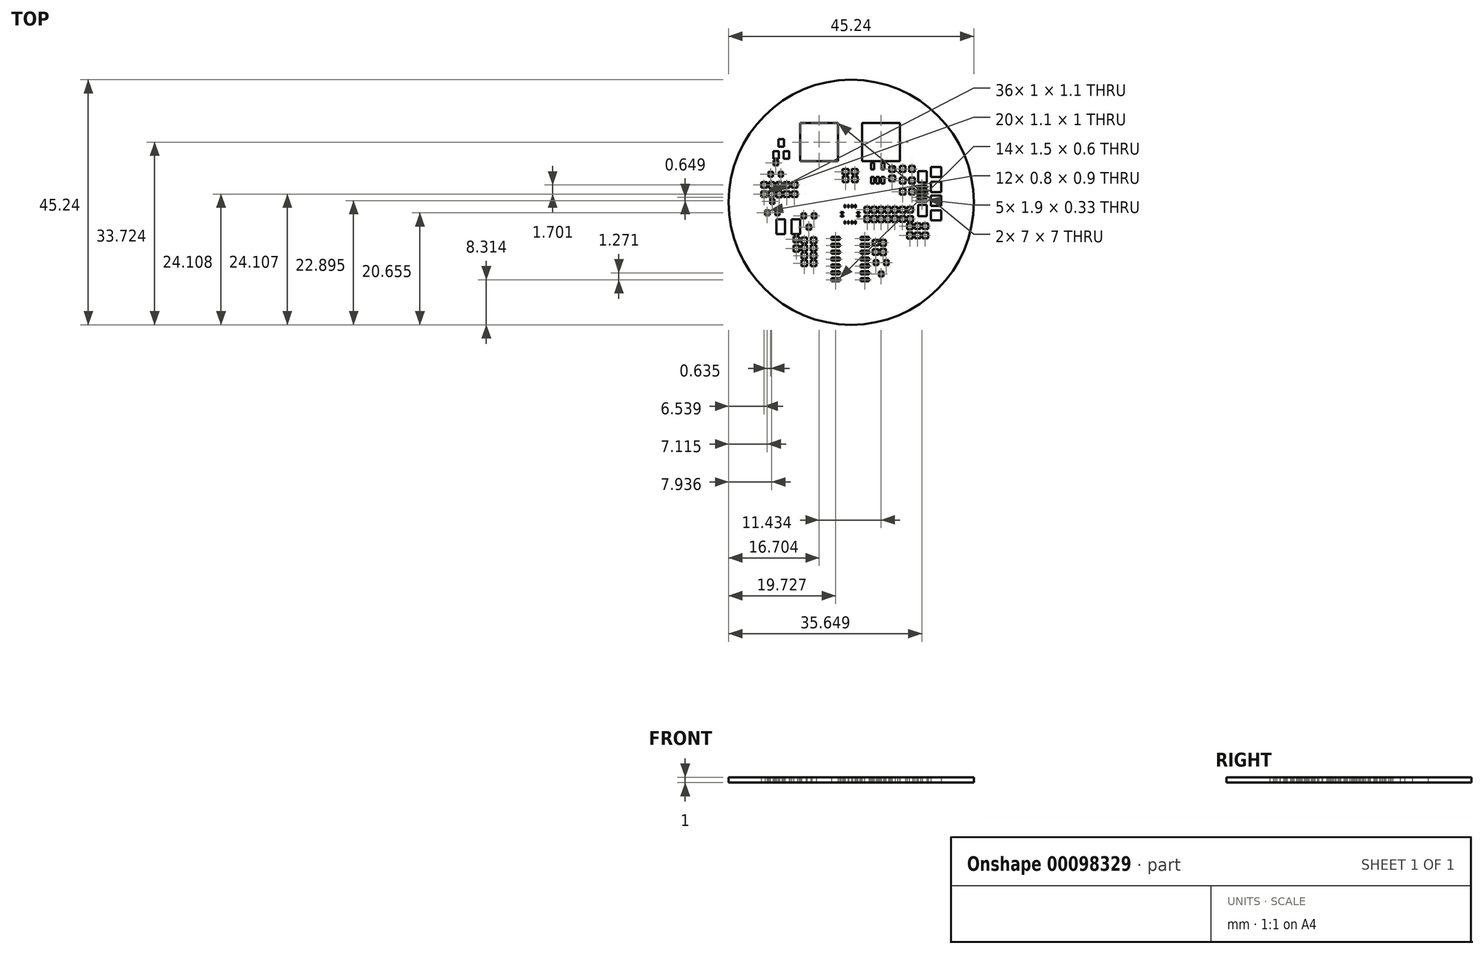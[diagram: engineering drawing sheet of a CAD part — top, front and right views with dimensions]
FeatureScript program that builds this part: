
annotation { "Feature Type Name" : "Feature", "Feature Type Description" : "" }
export const myFeature = defineFeature(function(context is Context, id is Id, definition is map)
    precondition{}
    {
        {
            var Q0;
            Q0=qCreatedBy(makeId("Top.planeOp"),FACE);
            var sketch = newSketch(context, id + "F0", { "sketchPlane" : qUnion([Q0])});
            skLineSegment(sketch, "E0", {"start": v(-10.61, -8) * mm, "end": v(-9.6, -8) * mm});
            skLineSegment(sketch, "E1", {"start": v(-9.6, -8) * mm, "end": v(-9.6, -9.1) * mm});
            skLineSegment(sketch, "E2", {"start": v(-9.6, -9.1) * mm, "end": v(-10.61, -9.1) * mm});
            skLineSegment(sketch, "E3", {"start": v(-10.61, -9.1) * mm, "end": v(-10.61, -8) * mm});
            skLineSegment(sketch, "E4", {"start": v(-9.17, -7.91) * mm, "end": v(-8.17, -7.91) * mm});
            skLineSegment(sketch, "E5", {"start": v(-8.17, -7.91) * mm, "end": v(-8.17, -9.01) * mm});
            skLineSegment(sketch, "E6", {"start": v(-8.17, -9.01) * mm, "end": v(-9.17, -9.01) * mm});
            skLineSegment(sketch, "E7", {"start": v(-9.17, -9.01) * mm, "end": v(-9.17, -7.91) * mm});
            skLineSegment(sketch, "E8", {"start": v(-9.17, -9.3) * mm, "end": v(-8.17, -9.3) * mm});
            skLineSegment(sketch, "E9", {"start": v(-8.17, -9.3) * mm, "end": v(-8.17, -10.4) * mm});
            skLineSegment(sketch, "E10", {"start": v(-8.17, -10.4) * mm, "end": v(-9.17, -10.4) * mm});
            skLineSegment(sketch, "E11", {"start": v(-9.17, -10.4) * mm, "end": v(-9.17, -9.3) * mm});
            skLineSegment(sketch, "E12", {"start": v(-9.17, -10.7) * mm, "end": v(-8.17, -10.7) * mm});
            skLineSegment(sketch, "E13", {"start": v(-8.17, -10.7) * mm, "end": v(-8.17, -11.8) * mm});
            skLineSegment(sketch, "E14", {"start": v(-8.17, -11.8) * mm, "end": v(-9.17, -11.8) * mm});
            skLineSegment(sketch, "E15", {"start": v(-9.17, -11.8) * mm, "end": v(-9.17, -10.7) * mm});
            skLineSegment(sketch, "E16", {"start": v(-7.47, -10.7) * mm, "end": v(-6.47, -10.7) * mm});
            skLineSegment(sketch, "E17", {"start": v(-6.47, -10.7) * mm, "end": v(-6.47, -11.8) * mm});
            skLineSegment(sketch, "E18", {"start": v(-6.47, -11.8) * mm, "end": v(-7.47, -11.8) * mm});
            skLineSegment(sketch, "E19", {"start": v(-7.47, -11.8) * mm, "end": v(-7.47, -10.7) * mm});
            skLineSegment(sketch, "E20", {"start": v(-7.47, -9.3) * mm, "end": v(-6.47, -9.3) * mm});
            skLineSegment(sketch, "E21", {"start": v(-6.47, -9.3) * mm, "end": v(-6.47, -10.4) * mm});
            skLineSegment(sketch, "E22", {"start": v(-6.47, -10.4) * mm, "end": v(-7.47, -10.4) * mm});
            skLineSegment(sketch, "E23", {"start": v(-7.47, -10.4) * mm, "end": v(-7.47, -9.3) * mm});
            skLineSegment(sketch, "E24", {"start": v(-7.47, -7.91) * mm, "end": v(-6.47, -7.91) * mm});
            skLineSegment(sketch, "E25", {"start": v(-6.47, -7.91) * mm, "end": v(-6.47, -9.01) * mm});
            skLineSegment(sketch, "E26", {"start": v(-6.47, -9.01) * mm, "end": v(-7.47, -9.01) * mm});
            skLineSegment(sketch, "E27", {"start": v(-7.47, -9.01) * mm, "end": v(-7.47, -7.91) * mm});
            skLineSegment(sketch, "E28", {"start": v(-7.47, -6.51) * mm, "end": v(-6.47, -6.51) * mm});
            skLineSegment(sketch, "E29", {"start": v(-6.47, -6.51) * mm, "end": v(-6.47, -7.61) * mm});
            skLineSegment(sketch, "E30", {"start": v(-6.47, -7.61) * mm, "end": v(-7.47, -7.61) * mm});
            skLineSegment(sketch, "E31", {"start": v(-7.47, -7.61) * mm, "end": v(-7.47, -6.51) * mm});
            skLineSegment(sketch, "E32", {"start": v(-9.17, -6.51) * mm, "end": v(-8.17, -6.51) * mm});
            skLineSegment(sketch, "E33", {"start": v(-8.17, -6.51) * mm, "end": v(-8.17, -7.61) * mm});
            skLineSegment(sketch, "E34", {"start": v(-8.17, -7.61) * mm, "end": v(-9.17, -7.61) * mm});
            skLineSegment(sketch, "E35", {"start": v(-9.17, -7.61) * mm, "end": v(-9.17, -6.51) * mm});
            skLineSegment(sketch, "E36", {"start": v(-10.61, -6.3) * mm, "end": v(-9.6, -6.3) * mm});
            skLineSegment(sketch, "E37", {"start": v(-9.6, -6.3) * mm, "end": v(-9.6, -7.4) * mm});
            skLineSegment(sketch, "E38", {"start": v(-9.6, -7.4) * mm, "end": v(-10.61, -7.4) * mm});
            skLineSegment(sketch, "E39", {"start": v(-10.61, -7.4) * mm, "end": v(-10.61, -6.3) * mm});
            skLineSegment(sketch, "E40", {"start": v(-13.79, 2.04) * mm, "end": v(-12.79, 2.04) * mm});
            skLineSegment(sketch, "E41", {"start": v(-12.79, 2.04) * mm, "end": v(-12.79, 0.94) * mm});
            skLineSegment(sketch, "E42", {"start": v(-12.79, 0.94) * mm, "end": v(-13.79, 0.94) * mm});
            skLineSegment(sketch, "E43", {"start": v(-13.79, 0.94) * mm, "end": v(-13.79, 2.04) * mm});
            skLineSegment(sketch, "E44", {"start": v(-15.18, 2.04) * mm, "end": v(-14.18, 2.04) * mm});
            skLineSegment(sketch, "E45", {"start": v(-14.18, 2.04) * mm, "end": v(-14.18, 0.94) * mm});
            skLineSegment(sketch, "E46", {"start": v(-14.18, 0.94) * mm, "end": v(-15.18, 0.94) * mm});
            skLineSegment(sketch, "E47", {"start": v(-15.18, 0.94) * mm, "end": v(-15.18, 2.04) * mm});
            skLineSegment(sketch, "E48", {"start": v(-15.18, 3.74) * mm, "end": v(-14.18, 3.74) * mm});
            skLineSegment(sketch, "E49", {"start": v(-14.18, 3.74) * mm, "end": v(-14.18, 2.64) * mm});
            skLineSegment(sketch, "E50", {"start": v(-14.18, 2.64) * mm, "end": v(-15.18, 2.64) * mm});
            skLineSegment(sketch, "E51", {"start": v(-15.18, 2.64) * mm, "end": v(-15.18, 3.74) * mm});
            skLineSegment(sketch, "E52", {"start": v(-13.79, 3.74) * mm, "end": v(-12.79, 3.74) * mm});
            skLineSegment(sketch, "E53", {"start": v(-12.79, 3.74) * mm, "end": v(-12.79, 2.64) * mm});
            skLineSegment(sketch, "E54", {"start": v(-12.79, 2.64) * mm, "end": v(-13.79, 2.64) * mm});
            skLineSegment(sketch, "E55", {"start": v(-13.79, 2.64) * mm, "end": v(-13.79, 3.74) * mm});
            skLineSegment(sketch, "E56", {"start": v(-1.55, 4.8) * mm, "end": v(-0.55, 4.8) * mm});
            skLineSegment(sketch, "E57", {"start": v(-0.55, 4.8) * mm, "end": v(-0.55, 3.7) * mm});
            skLineSegment(sketch, "E58", {"start": v(-0.55, 3.7) * mm, "end": v(-1.55, 3.7) * mm});
            skLineSegment(sketch, "E59", {"start": v(-1.55, 3.7) * mm, "end": v(-1.55, 4.8) * mm});
            skLineSegment(sketch, "E60", {"start": v(0.15, 4.8) * mm, "end": v(1.15, 4.8) * mm});
            skLineSegment(sketch, "E61", {"start": v(1.15, 4.8) * mm, "end": v(1.15, 3.7) * mm});
            skLineSegment(sketch, "E62", {"start": v(1.15, 3.7) * mm, "end": v(0.15, 3.7) * mm});
            skLineSegment(sketch, "E63", {"start": v(0.15, 3.7) * mm, "end": v(0.15, 4.8) * mm});
            skLineSegment(sketch, "E64", {"start": v(2.48, -0.84) * mm, "end": v(3.48, -0.84) * mm});
            skLineSegment(sketch, "E65", {"start": v(3.48, -0.84) * mm, "end": v(3.48, -1.94) * mm});
            skLineSegment(sketch, "E66", {"start": v(3.48, -1.94) * mm, "end": v(2.48, -1.94) * mm});
            skLineSegment(sketch, "E67", {"start": v(2.48, -1.94) * mm, "end": v(2.48, -0.84) * mm});
            skLineSegment(sketch, "E68", {"start": v(3.75, -0.84) * mm, "end": v(4.75, -0.84) * mm});
            skLineSegment(sketch, "E69", {"start": v(4.75, -0.84) * mm, "end": v(4.75, -1.94) * mm});
            skLineSegment(sketch, "E70", {"start": v(4.75, -1.94) * mm, "end": v(3.75, -1.94) * mm});
            skLineSegment(sketch, "E71", {"start": v(3.75, -1.94) * mm, "end": v(3.75, -0.84) * mm});
            skLineSegment(sketch, "E72", {"start": v(5.02, -0.84) * mm, "end": v(6.02, -0.84) * mm});
            skLineSegment(sketch, "E73", {"start": v(6.02, -0.84) * mm, "end": v(6.02, -1.94) * mm});
            skLineSegment(sketch, "E74", {"start": v(6.02, -1.94) * mm, "end": v(5.02, -1.94) * mm});
            skLineSegment(sketch, "E75", {"start": v(5.02, -1.94) * mm, "end": v(5.02, -0.84) * mm});
            skLineSegment(sketch, "E76", {"start": v(6.29, -0.84) * mm, "end": v(7.29, -0.84) * mm});
            skLineSegment(sketch, "E77", {"start": v(7.29, -0.84) * mm, "end": v(7.29, -1.94) * mm});
            skLineSegment(sketch, "E78", {"start": v(7.29, -1.94) * mm, "end": v(6.29, -1.94) * mm});
            skLineSegment(sketch, "E79", {"start": v(6.29, -1.94) * mm, "end": v(6.29, -0.84) * mm});
            skLineSegment(sketch, "E80", {"start": v(7.56, -0.84) * mm, "end": v(8.56, -0.84) * mm});
            skLineSegment(sketch, "E81", {"start": v(8.56, -0.84) * mm, "end": v(8.56, -1.94) * mm});
            skLineSegment(sketch, "E82", {"start": v(8.56, -1.94) * mm, "end": v(7.56, -1.94) * mm});
            skLineSegment(sketch, "E83", {"start": v(7.56, -1.94) * mm, "end": v(7.56, -0.84) * mm});
            skLineSegment(sketch, "E84", {"start": v(7.56, -2.54) * mm, "end": v(8.56, -2.54) * mm});
            skLineSegment(sketch, "E85", {"start": v(8.56, -2.54) * mm, "end": v(8.56, -3.64) * mm});
            skLineSegment(sketch, "E86", {"start": v(8.56, -3.64) * mm, "end": v(7.56, -3.64) * mm});
            skLineSegment(sketch, "E87", {"start": v(7.56, -3.64) * mm, "end": v(7.56, -2.54) * mm});
            skLineSegment(sketch, "E88", {"start": v(6.29, -2.54) * mm, "end": v(7.29, -2.54) * mm});
            skLineSegment(sketch, "E89", {"start": v(7.29, -2.54) * mm, "end": v(7.29, -3.64) * mm});
            skLineSegment(sketch, "E90", {"start": v(7.29, -3.64) * mm, "end": v(6.29, -3.64) * mm});
            skLineSegment(sketch, "E91", {"start": v(6.29, -3.64) * mm, "end": v(6.29, -2.54) * mm});
            skLineSegment(sketch, "E92", {"start": v(5.02, -2.54) * mm, "end": v(6.02, -2.54) * mm});
            skLineSegment(sketch, "E93", {"start": v(6.02, -2.54) * mm, "end": v(6.02, -3.64) * mm});
            skLineSegment(sketch, "E94", {"start": v(6.02, -3.64) * mm, "end": v(5.02, -3.64) * mm});
            skLineSegment(sketch, "E95", {"start": v(5.02, -3.64) * mm, "end": v(5.02, -2.54) * mm});
            skLineSegment(sketch, "E96", {"start": v(3.75, -2.54) * mm, "end": v(4.75, -2.54) * mm});
            skLineSegment(sketch, "E97", {"start": v(4.75, -2.54) * mm, "end": v(4.75, -3.64) * mm});
            skLineSegment(sketch, "E98", {"start": v(4.75, -3.64) * mm, "end": v(3.75, -3.64) * mm});
            skLineSegment(sketch, "E99", {"start": v(3.75, -3.64) * mm, "end": v(3.75, -2.54) * mm});
            skLineSegment(sketch, "E100", {"start": v(2.48, -2.54) * mm, "end": v(3.48, -2.54) * mm});
            skLineSegment(sketch, "E101", {"start": v(3.48, -2.54) * mm, "end": v(3.48, -3.64) * mm});
            skLineSegment(sketch, "E102", {"start": v(3.48, -3.64) * mm, "end": v(2.48, -3.64) * mm});
            skLineSegment(sketch, "E103", {"start": v(2.48, -3.64) * mm, "end": v(2.48, -2.54) * mm});
            skLineSegment(sketch, "E104", {"start": v(5.4, -6.93) * mm, "end": v(6.4, -6.93) * mm});
            skLineSegment(sketch, "E105", {"start": v(6.4, -6.93) * mm, "end": v(6.4, -8.03) * mm});
            skLineSegment(sketch, "E106", {"start": v(6.4, -8.03) * mm, "end": v(5.4, -8.03) * mm});
            skLineSegment(sketch, "E107", {"start": v(5.4, -8.03) * mm, "end": v(5.4, -6.93) * mm});
            skLineSegment(sketch, "E108", {"start": v(5.4, -8.63) * mm, "end": v(6.4, -8.63) * mm});
            skLineSegment(sketch, "E109", {"start": v(6.4, -8.63) * mm, "end": v(6.4, -9.73) * mm});
            skLineSegment(sketch, "E110", {"start": v(6.4, -9.73) * mm, "end": v(5.4, -9.73) * mm});
            skLineSegment(sketch, "E111", {"start": v(5.4, -9.73) * mm, "end": v(5.4, -8.63) * mm});
            skLineSegment(sketch, "E112", {"start": v(10.35, -5.59) * mm, "end": v(11.35, -5.59) * mm});
            skLineSegment(sketch, "E113", {"start": v(11.35, -5.59) * mm, "end": v(11.35, -6.69) * mm});
            skLineSegment(sketch, "E114", {"start": v(11.35, -6.69) * mm, "end": v(10.35, -6.69) * mm});
            skLineSegment(sketch, "E115", {"start": v(10.35, -6.69) * mm, "end": v(10.35, -5.59) * mm});
            skLineSegment(sketch, "E116", {"start": v(10.35, -3.88) * mm, "end": v(11.35, -3.88) * mm});
            skLineSegment(sketch, "E117", {"start": v(11.35, -3.88) * mm, "end": v(11.35, -4.98) * mm});
            skLineSegment(sketch, "E118", {"start": v(11.35, -4.98) * mm, "end": v(10.35, -4.98) * mm});
            skLineSegment(sketch, "E119", {"start": v(10.35, -4.98) * mm, "end": v(10.35, -3.88) * mm});
            skLineSegment(sketch, "E120", {"start": v(10.7, 2.5) * mm, "end": v(11.7, 2.5) * mm});
            skLineSegment(sketch, "E121", {"start": v(11.7, 2.5) * mm, "end": v(11.7, 1.4) * mm});
            skLineSegment(sketch, "E122", {"start": v(11.7, 1.4) * mm, "end": v(10.7, 1.4) * mm});
            skLineSegment(sketch, "E123", {"start": v(10.7, 1.4) * mm, "end": v(10.7, 2.5) * mm});
            skLineSegment(sketch, "E124", {"start": v(9, 2.5) * mm, "end": v(10, 2.5) * mm});
            skLineSegment(sketch, "E125", {"start": v(10, 2.5) * mm, "end": v(10, 1.4) * mm});
            skLineSegment(sketch, "E126", {"start": v(10, 1.4) * mm, "end": v(9, 1.4) * mm});
            skLineSegment(sketch, "E127", {"start": v(9, 1.4) * mm, "end": v(9, 2.5) * mm});
            skLineSegment(sketch, "E128", {"start": v(9, 4.54) * mm, "end": v(10, 4.54) * mm});
            skLineSegment(sketch, "E129", {"start": v(10, 4.54) * mm, "end": v(10, 3.44) * mm});
            skLineSegment(sketch, "E130", {"start": v(10, 3.44) * mm, "end": v(9, 3.44) * mm});
            skLineSegment(sketch, "E131", {"start": v(9, 3.44) * mm, "end": v(9, 4.54) * mm});
            skLineSegment(sketch, "E132", {"start": v(10.7, 4.54) * mm, "end": v(11.7, 4.54) * mm});
            skLineSegment(sketch, "E133", {"start": v(11.7, 4.54) * mm, "end": v(11.7, 3.44) * mm});
            skLineSegment(sketch, "E134", {"start": v(11.7, 3.44) * mm, "end": v(10.7, 3.44) * mm});
            skLineSegment(sketch, "E135", {"start": v(10.7, 3.44) * mm, "end": v(10.7, 4.54) * mm});
            skLineSegment(sketch, "E136", {"start": v(10.7, 6.7) * mm, "end": v(11.7, 6.7) * mm});
            skLineSegment(sketch, "E137", {"start": v(11.7, 6.7) * mm, "end": v(11.7, 5.6) * mm});
            skLineSegment(sketch, "E138", {"start": v(11.7, 5.6) * mm, "end": v(10.7, 5.6) * mm});
            skLineSegment(sketch, "E139", {"start": v(10.7, 5.6) * mm, "end": v(10.7, 6.7) * mm});
            skLineSegment(sketch, "E140", {"start": v(9, 6.7) * mm, "end": v(10, 6.7) * mm});
            skLineSegment(sketch, "E141", {"start": v(10, 6.7) * mm, "end": v(10, 5.6) * mm});
            skLineSegment(sketch, "E142", {"start": v(10, 5.6) * mm, "end": v(9, 5.6) * mm});
            skLineSegment(sketch, "E143", {"start": v(9, 5.6) * mm, "end": v(9, 6.7) * mm});
            skLineSegment(sketch, "E144", {"start": v(7, 6.61) * mm, "end": v(8.1, 6.61) * mm});
            skLineSegment(sketch, "E145", {"start": v(8.1, 6.61) * mm, "end": v(8.1, 5.61) * mm});
            skLineSegment(sketch, "E146", {"start": v(8.1, 5.61) * mm, "end": v(7, 5.61) * mm});
            skLineSegment(sketch, "E147", {"start": v(7, 5.61) * mm, "end": v(7, 6.61) * mm});
            skLineSegment(sketch, "E148", {"start": v(7, 4.91) * mm, "end": v(8.1, 4.91) * mm});
            skLineSegment(sketch, "E149", {"start": v(8.1, 4.91) * mm, "end": v(8.1, 3.9) * mm});
            skLineSegment(sketch, "E150", {"start": v(8.1, 3.9) * mm, "end": v(7, 3.9) * mm});
            skLineSegment(sketch, "E151", {"start": v(7, 3.9) * mm, "end": v(7, 4.91) * mm});
            skLineSegment(sketch, "E152", {"start": v(8.9, -0.88) * mm, "end": v(10, -0.88) * mm});
            skLineSegment(sketch, "E153", {"start": v(10, -0.88) * mm, "end": v(10, -1.89) * mm});
            skLineSegment(sketch, "E154", {"start": v(10, -1.89) * mm, "end": v(8.9, -1.89) * mm});
            skLineSegment(sketch, "E155", {"start": v(8.9, -1.89) * mm, "end": v(8.9, -0.88) * mm});
            skLineSegment(sketch, "E156", {"start": v(10.3, -0.88) * mm, "end": v(11.4, -0.88) * mm});
            skLineSegment(sketch, "E157", {"start": v(11.4, -0.88) * mm, "end": v(11.4, -1.89) * mm});
            skLineSegment(sketch, "E158", {"start": v(11.4, -1.89) * mm, "end": v(10.3, -1.89) * mm});
            skLineSegment(sketch, "E159", {"start": v(10.3, -1.89) * mm, "end": v(10.3, -0.88) * mm});
            skLineSegment(sketch, "E160", {"start": v(10.3, -2.58) * mm, "end": v(11.4, -2.58) * mm});
            skLineSegment(sketch, "E161", {"start": v(11.4, -2.58) * mm, "end": v(11.4, -3.59) * mm});
            skLineSegment(sketch, "E162", {"start": v(11.4, -3.59) * mm, "end": v(10.3, -3.59) * mm});
            skLineSegment(sketch, "E163", {"start": v(10.3, -3.59) * mm, "end": v(10.3, -2.58) * mm});
            skLineSegment(sketch, "E164", {"start": v(8.9, -2.58) * mm, "end": v(10, -2.58) * mm});
            skLineSegment(sketch, "E165", {"start": v(10, -2.58) * mm, "end": v(10, -3.59) * mm});
            skLineSegment(sketch, "E166", {"start": v(10, -3.59) * mm, "end": v(8.9, -3.59) * mm});
            skLineSegment(sketch, "E167", {"start": v(8.9, -3.59) * mm, "end": v(8.9, -2.58) * mm});
            skLineSegment(sketch, "E168", {"start": v(11.7, -3.93) * mm, "end": v(12.8, -3.93) * mm});
            skLineSegment(sketch, "E169", {"start": v(12.8, -3.93) * mm, "end": v(12.8, -4.94) * mm});
            skLineSegment(sketch, "E170", {"start": v(12.8, -4.94) * mm, "end": v(11.7, -4.94) * mm});
            skLineSegment(sketch, "E171", {"start": v(11.7, -4.94) * mm, "end": v(11.7, -3.93) * mm});
            skLineSegment(sketch, "E172", {"start": v(13.1, -3.93) * mm, "end": v(14.2, -3.93) * mm});
            skLineSegment(sketch, "E173", {"start": v(14.2, -3.93) * mm, "end": v(14.2, -4.94) * mm});
            skLineSegment(sketch, "E174", {"start": v(14.2, -4.94) * mm, "end": v(13.1, -4.94) * mm});
            skLineSegment(sketch, "E175", {"start": v(13.1, -4.94) * mm, "end": v(13.1, -3.93) * mm});
            skLineSegment(sketch, "E176", {"start": v(13.1, -5.63) * mm, "end": v(14.2, -5.63) * mm});
            skLineSegment(sketch, "E177", {"start": v(14.2, -5.63) * mm, "end": v(14.2, -6.63) * mm});
            skLineSegment(sketch, "E178", {"start": v(14.2, -6.63) * mm, "end": v(13.1, -6.63) * mm});
            skLineSegment(sketch, "E179", {"start": v(13.1, -6.63) * mm, "end": v(13.1, -5.63) * mm});
            skLineSegment(sketch, "E180", {"start": v(11.7, -5.63) * mm, "end": v(12.8, -5.63) * mm});
            skLineSegment(sketch, "E181", {"start": v(12.8, -5.63) * mm, "end": v(12.8, -6.63) * mm});
            skLineSegment(sketch, "E182", {"start": v(12.8, -6.63) * mm, "end": v(11.7, -6.63) * mm});
            skLineSegment(sketch, "E183", {"start": v(11.7, -6.63) * mm, "end": v(11.7, -5.63) * mm});
            skLineSegment(sketch, "E184", {"start": v(3.95, -6.98) * mm, "end": v(5.05, -6.98) * mm});
            skLineSegment(sketch, "E185", {"start": v(5.05, -6.98) * mm, "end": v(5.05, -7.98) * mm});
            skLineSegment(sketch, "E186", {"start": v(5.05, -7.98) * mm, "end": v(3.95, -7.98) * mm});
            skLineSegment(sketch, "E187", {"start": v(3.95, -7.98) * mm, "end": v(3.95, -6.98) * mm});
            skLineSegment(sketch, "E188", {"start": v(3.95, -8.68) * mm, "end": v(5.05, -8.68) * mm});
            skLineSegment(sketch, "E189", {"start": v(5.05, -8.68) * mm, "end": v(5.05, -9.68) * mm});
            skLineSegment(sketch, "E190", {"start": v(5.05, -9.68) * mm, "end": v(3.95, -9.68) * mm});
            skLineSegment(sketch, "E191", {"start": v(3.95, -9.68) * mm, "end": v(3.95, -8.68) * mm});
            skLineSegment(sketch, "E192", {"start": v(-11.04, 1.99) * mm, "end": v(-9.94, 1.99) * mm});
            skLineSegment(sketch, "E193", {"start": v(-9.94, 1.99) * mm, "end": v(-9.94, 0.99) * mm});
            skLineSegment(sketch, "E194", {"start": v(-9.94, 0.99) * mm, "end": v(-11.04, 0.99) * mm});
            skLineSegment(sketch, "E195", {"start": v(-11.04, 0.99) * mm, "end": v(-11.04, 1.99) * mm});
            skLineSegment(sketch, "E196", {"start": v(-12.44, 1.99) * mm, "end": v(-11.34, 1.99) * mm});
            skLineSegment(sketch, "E197", {"start": v(-11.34, 1.99) * mm, "end": v(-11.34, 0.99) * mm});
            skLineSegment(sketch, "E198", {"start": v(-11.34, 0.99) * mm, "end": v(-12.44, 0.99) * mm});
            skLineSegment(sketch, "E199", {"start": v(-12.44, 0.99) * mm, "end": v(-12.44, 1.99) * mm});
            skLineSegment(sketch, "E200", {"start": v(-12.44, 3.69) * mm, "end": v(-11.34, 3.69) * mm});
            skLineSegment(sketch, "E201", {"start": v(-11.34, 3.69) * mm, "end": v(-11.34, 2.69) * mm});
            skLineSegment(sketch, "E202", {"start": v(-11.34, 2.69) * mm, "end": v(-12.44, 2.69) * mm});
            skLineSegment(sketch, "E203", {"start": v(-12.44, 2.69) * mm, "end": v(-12.44, 3.69) * mm});
            skLineSegment(sketch, "E204", {"start": v(-11.04, 3.69) * mm, "end": v(-9.94, 3.69) * mm});
            skLineSegment(sketch, "E205", {"start": v(-9.94, 3.69) * mm, "end": v(-9.94, 2.69) * mm});
            skLineSegment(sketch, "E206", {"start": v(-9.94, 2.69) * mm, "end": v(-11.04, 2.69) * mm});
            skLineSegment(sketch, "E207", {"start": v(-11.04, 2.69) * mm, "end": v(-11.04, 3.69) * mm});
            skLineSegment(sketch, "E208", {"start": v(-16.63, 3.69) * mm, "end": v(-15.53, 3.69) * mm});
            skLineSegment(sketch, "E209", {"start": v(-15.53, 3.69) * mm, "end": v(-15.53, 2.69) * mm});
            skLineSegment(sketch, "E210", {"start": v(-15.53, 2.69) * mm, "end": v(-16.63, 2.69) * mm});
            skLineSegment(sketch, "E211", {"start": v(-16.63, 2.69) * mm, "end": v(-16.63, 3.69) * mm});
            skLineSegment(sketch, "E212", {"start": v(-16.63, 1.99) * mm, "end": v(-15.53, 1.99) * mm});
            skLineSegment(sketch, "E213", {"start": v(-15.53, 1.99) * mm, "end": v(-15.53, 0.99) * mm});
            skLineSegment(sketch, "E214", {"start": v(-15.53, 0.99) * mm, "end": v(-16.63, 0.99) * mm});
            skLineSegment(sketch, "E215", {"start": v(-16.63, 0.99) * mm, "end": v(-16.63, 1.99) * mm});
            skLineSegment(sketch, "E216", {"start": v(-1.6, 6.14) * mm, "end": v(-0.5, 6.14) * mm});
            skLineSegment(sketch, "E217", {"start": v(-0.5, 6.14) * mm, "end": v(-0.5, 5.14) * mm});
            skLineSegment(sketch, "E218", {"start": v(-0.5, 5.14) * mm, "end": v(-1.6, 5.14) * mm});
            skLineSegment(sketch, "E219", {"start": v(-1.6, 5.14) * mm, "end": v(-1.6, 6.14) * mm});
            skLineSegment(sketch, "E220", {"start": v(0.1, 6.14) * mm, "end": v(1.2, 6.14) * mm});
            skLineSegment(sketch, "E221", {"start": v(1.2, 6.14) * mm, "end": v(1.2, 5.14) * mm});
            skLineSegment(sketch, "E222", {"start": v(1.2, 5.14) * mm, "end": v(0.1, 5.14) * mm});
            skLineSegment(sketch, "E223", {"start": v(0.1, 5.14) * mm, "end": v(0.1, 6.14) * mm});
            skLineSegment(sketch, "E224", {"start": v(1.56, -2.64) * mm, "end": v(1.04, -2.64) * mm});
            skLineSegment(sketch, "E225", {"start": v(1.04, -2.64) * mm, "end": v(1.04, -2.48) * mm});
            skLineSegment(sketch, "E226", {"start": v(1.04, -2.48) * mm, "end": v(1.56, -2.48) * mm});
            skLineSegment(sketch, "E227", {"start": v(1.56, -2.48) * mm, "end": v(1.56, -2.64) * mm});
            skLineSegment(sketch, "E228", {"start": v(1.56, -2) * mm, "end": v(1.04, -2) * mm});
            skLineSegment(sketch, "E229", {"start": v(1.04, -2) * mm, "end": v(1.04, -1.83) * mm});
            skLineSegment(sketch, "E230", {"start": v(1.04, -1.83) * mm, "end": v(1.56, -1.83) * mm});
            skLineSegment(sketch, "E231", {"start": v(1.56, -1.83) * mm, "end": v(1.56, -2) * mm});
            skLineSegment(sketch, "E232", {"start": v(0.7, -1) * mm, "end": v(0.7, -0.47) * mm});
            skLineSegment(sketch, "E233", {"start": v(0.7, -0.47) * mm, "end": v(0.86, -0.47) * mm});
            skLineSegment(sketch, "E234", {"start": v(0.86, -0.47) * mm, "end": v(0.86, -1) * mm});
            skLineSegment(sketch, "E235", {"start": v(0.86, -1) * mm, "end": v(0.7, -1) * mm});
            skLineSegment(sketch, "E236", {"start": v(0.7, -0.83) * mm, "end": v(0.86, -0.83) * mm});
            skLineSegment(sketch, "E237", {"start": v(0.86, -0.67) * mm, "end": v(0.7, -0.67) * mm});
            skLineSegment(sketch, "E238", {"start": v(0.7, -0.5) * mm, "end": v(0.86, -0.5) * mm});
            skLineSegment(sketch, "E239", {"start": v(0.04, -0.47) * mm, "end": v(0.04, -1) * mm});
            skLineSegment(sketch, "E240", {"start": v(0.04, -0.47) * mm, "end": v(0.2, -0.47) * mm});
            skLineSegment(sketch, "E241", {"start": v(0.2, -0.47) * mm, "end": v(0.2, -1) * mm});
            skLineSegment(sketch, "E242", {"start": v(0.2, -1) * mm, "end": v(0.04, -1) * mm});
            skLineSegment(sketch, "E243", {"start": v(0.04, -0.83) * mm, "end": v(0.2, -0.83) * mm});
            skLineSegment(sketch, "E244", {"start": v(0.2, -0.67) * mm, "end": v(0.04, -0.67) * mm});
            skLineSegment(sketch, "E245", {"start": v(0.04, -0.5) * mm, "end": v(0.2, -0.5) * mm});
            skLineSegment(sketch, "E246", {"start": v(-0.6, -0.47) * mm, "end": v(-0.6, -1) * mm});
            skLineSegment(sketch, "E247", {"start": v(-0.6, -0.47) * mm, "end": v(-0.44, -0.47) * mm});
            skLineSegment(sketch, "E248", {"start": v(-0.44, -0.47) * mm, "end": v(-0.44, -1) * mm});
            skLineSegment(sketch, "E249", {"start": v(-0.44, -1) * mm, "end": v(-0.6, -1) * mm});
            skLineSegment(sketch, "E250", {"start": v(-0.6, -0.83) * mm, "end": v(-0.44, -0.83) * mm});
            skLineSegment(sketch, "E251", {"start": v(-0.44, -0.67) * mm, "end": v(-0.6, -0.67) * mm});
            skLineSegment(sketch, "E252", {"start": v(-0.6, -0.5) * mm, "end": v(-0.44, -0.5) * mm});
            skLineSegment(sketch, "E253", {"start": v(-1.26, -0.47) * mm, "end": v(-1.26, -1) * mm});
            skLineSegment(sketch, "E254", {"start": v(-1.26, -0.47) * mm, "end": v(-1.1, -0.47) * mm});
            skLineSegment(sketch, "E255", {"start": v(-1.1, -0.47) * mm, "end": v(-1.1, -1) * mm});
            skLineSegment(sketch, "E256", {"start": v(-1.1, -1) * mm, "end": v(-1.26, -1) * mm});
            skLineSegment(sketch, "E257", {"start": v(-1.26, -0.83) * mm, "end": v(-1.1, -0.83) * mm});
            skLineSegment(sketch, "E258", {"start": v(-1.1, -0.67) * mm, "end": v(-1.26, -0.67) * mm});
            skLineSegment(sketch, "E259", {"start": v(-1.26, -0.5) * mm, "end": v(-1.1, -0.5) * mm});
            skLineSegment(sketch, "E260", {"start": v(-1.44, -2) * mm, "end": v(-1.96, -2) * mm});
            skLineSegment(sketch, "E261", {"start": v(-1.96, -2) * mm, "end": v(-1.96, -1.83) * mm});
            skLineSegment(sketch, "E262", {"start": v(-1.96, -1.83) * mm, "end": v(-1.44, -1.83) * mm});
            skLineSegment(sketch, "E263", {"start": v(-1.44, -1.83) * mm, "end": v(-1.44, -2) * mm});
            skLineSegment(sketch, "E264", {"start": v(-1.44, -2.64) * mm, "end": v(-1.96, -2.64) * mm});
            skLineSegment(sketch, "E265", {"start": v(-1.96, -2.64) * mm, "end": v(-1.96, -2.48) * mm});
            skLineSegment(sketch, "E266", {"start": v(-1.96, -2.48) * mm, "end": v(-1.44, -2.48) * mm});
            skLineSegment(sketch, "E267", {"start": v(-1.44, -2.48) * mm, "end": v(-1.44, -2.64) * mm});
            skLineSegment(sketch, "E268", {"start": v(-1.26, -3.48) * mm, "end": v(-1.26, -4) * mm});
            skLineSegment(sketch, "E269", {"start": v(-1.26, -3.48) * mm, "end": v(-1.1, -3.48) * mm});
            skLineSegment(sketch, "E270", {"start": v(-1.1, -3.48) * mm, "end": v(-1.1, -4) * mm});
            skLineSegment(sketch, "E271", {"start": v(-1.1, -4) * mm, "end": v(-1.26, -4) * mm});
            skLineSegment(sketch, "E272", {"start": v(-1.26, -3.83) * mm, "end": v(-1.1, -3.83) * mm});
            skLineSegment(sketch, "E273", {"start": v(-1.1, -3.67) * mm, "end": v(-1.26, -3.67) * mm});
            skLineSegment(sketch, "E274", {"start": v(-1.26, -3.5) * mm, "end": v(-1.1, -3.5) * mm});
            skLineSegment(sketch, "E275", {"start": v(-0.6, -3.48) * mm, "end": v(-0.6, -4) * mm});
            skLineSegment(sketch, "E276", {"start": v(-0.6, -3.48) * mm, "end": v(-0.44, -3.48) * mm});
            skLineSegment(sketch, "E277", {"start": v(-0.44, -3.48) * mm, "end": v(-0.44, -4) * mm});
            skLineSegment(sketch, "E278", {"start": v(-0.44, -4) * mm, "end": v(-0.6, -4) * mm});
            skLineSegment(sketch, "E279", {"start": v(-0.6, -3.83) * mm, "end": v(-0.44, -3.83) * mm});
            skLineSegment(sketch, "E280", {"start": v(-0.44, -3.67) * mm, "end": v(-0.6, -3.67) * mm});
            skLineSegment(sketch, "E281", {"start": v(-0.6, -3.5) * mm, "end": v(-0.44, -3.5) * mm});
            skLineSegment(sketch, "E282", {"start": v(0.04, -3.48) * mm, "end": v(0.04, -4) * mm});
            skLineSegment(sketch, "E283", {"start": v(0.04, -3.48) * mm, "end": v(0.2, -3.48) * mm});
            skLineSegment(sketch, "E284", {"start": v(0.2, -3.48) * mm, "end": v(0.2, -4) * mm});
            skLineSegment(sketch, "E285", {"start": v(0.2, -4) * mm, "end": v(0.04, -4) * mm});
            skLineSegment(sketch, "E286", {"start": v(0.04, -3.83) * mm, "end": v(0.2, -3.83) * mm});
            skLineSegment(sketch, "E287", {"start": v(0.2, -3.67) * mm, "end": v(0.04, -3.67) * mm});
            skLineSegment(sketch, "E288", {"start": v(0.04, -3.5) * mm, "end": v(0.2, -3.5) * mm});
            skLineSegment(sketch, "E289", {"start": v(0.7, -3.48) * mm, "end": v(0.7, -4) * mm});
            skLineSegment(sketch, "E290", {"start": v(0.7, -3.48) * mm, "end": v(0.86, -3.48) * mm});
            skLineSegment(sketch, "E291", {"start": v(0.86, -3.48) * mm, "end": v(0.86, -4) * mm});
            skLineSegment(sketch, "E292", {"start": v(0.86, -4) * mm, "end": v(0.7, -4) * mm});
            skLineSegment(sketch, "E293", {"start": v(0.7, -3.83) * mm, "end": v(0.86, -3.83) * mm});
            skLineSegment(sketch, "E294", {"start": v(0.86, -3.67) * mm, "end": v(0.7, -3.67) * mm});
            skLineSegment(sketch, "E295", {"start": v(0.7, -3.5) * mm, "end": v(0.86, -3.5) * mm});
            skLineSegment(sketch, "E296", {"start": v(-11.03, -3.17) * mm, "end": v(-9.43, -3.17) * mm});
            skLineSegment(sketch, "E297", {"start": v(-9.43, -3.17) * mm, "end": v(-9.43, -5.87) * mm});
            skLineSegment(sketch, "E298", {"start": v(-9.43, -5.87) * mm, "end": v(-11.03, -5.87) * mm});
            skLineSegment(sketch, "E299", {"start": v(-11.03, -5.87) * mm, "end": v(-11.03, -3.17) * mm});
            skLineSegment(sketch, "E300", {"start": v(-13.83, -3.17) * mm, "end": v(-12.23, -3.17) * mm});
            skLineSegment(sketch, "E301", {"start": v(-12.23, -3.17) * mm, "end": v(-12.23, -5.87) * mm});
            skLineSegment(sketch, "E302", {"start": v(-12.23, -5.87) * mm, "end": v(-13.83, -5.87) * mm});
            skLineSegment(sketch, "E303", {"start": v(-13.83, -5.87) * mm, "end": v(-13.83, -3.17) * mm});
            skLineSegment(sketch, "E304", {"start": v(-14, -1.52) * mm, "end": v(-13.2, -1.52) * mm});
            skLineSegment(sketch, "E305", {"start": v(-13.2, -1.52) * mm, "end": v(-13.2, -2.42) * mm});
            skLineSegment(sketch, "E306", {"start": v(-13.2, -2.42) * mm, "end": v(-14, -2.42) * mm});
            skLineSegment(sketch, "E307", {"start": v(-14, -2.42) * mm, "end": v(-14, -1.52) * mm});
            skLineSegment(sketch, "E308", {"start": v(-15.9, -1.52) * mm, "end": v(-15.1, -1.52) * mm});
            skLineSegment(sketch, "E309", {"start": v(-15.1, -1.52) * mm, "end": v(-15.1, -2.42) * mm});
            skLineSegment(sketch, "E310", {"start": v(-15.1, -2.42) * mm, "end": v(-15.9, -2.42) * mm});
            skLineSegment(sketch, "E311", {"start": v(-15.9, -2.42) * mm, "end": v(-15.9, -1.52) * mm});
            skLineSegment(sketch, "E312", {"start": v(-14.96, 0.59) * mm, "end": v(-14.16, 0.59) * mm});
            skLineSegment(sketch, "E313", {"start": v(-14.16, 0.59) * mm, "end": v(-14.16, -0.31) * mm});
            skLineSegment(sketch, "E314", {"start": v(-14.16, -0.31) * mm, "end": v(-14.96, -0.31) * mm});
            skLineSegment(sketch, "E315", {"start": v(-14.96, -0.31) * mm, "end": v(-14.96, 0.59) * mm});
            skLineSegment(sketch, "E316", {"start": v(-15.27, 5.6) * mm, "end": v(-14.47, 5.6) * mm});
            skLineSegment(sketch, "E317", {"start": v(-14.47, 5.6) * mm, "end": v(-14.47, 4.7) * mm});
            skLineSegment(sketch, "E318", {"start": v(-14.47, 4.7) * mm, "end": v(-15.27, 4.7) * mm});
            skLineSegment(sketch, "E319", {"start": v(-15.27, 4.7) * mm, "end": v(-15.27, 5.6) * mm});
            skLineSegment(sketch, "E320", {"start": v(-13.37, 5.6) * mm, "end": v(-12.57, 5.6) * mm});
            skLineSegment(sketch, "E321", {"start": v(-12.57, 5.6) * mm, "end": v(-12.57, 4.7) * mm});
            skLineSegment(sketch, "E322", {"start": v(-12.57, 4.7) * mm, "end": v(-13.37, 4.7) * mm});
            skLineSegment(sketch, "E323", {"start": v(-13.37, 4.7) * mm, "end": v(-13.37, 5.6) * mm});
            skLineSegment(sketch, "E324", {"start": v(-14.32, 7.7) * mm, "end": v(-13.52, 7.7) * mm});
            skLineSegment(sketch, "E325", {"start": v(-13.52, 7.7) * mm, "end": v(-13.52, 6.8) * mm});
            skLineSegment(sketch, "E326", {"start": v(-13.52, 6.8) * mm, "end": v(-14.32, 6.8) * mm});
            skLineSegment(sketch, "E327", {"start": v(-14.32, 6.8) * mm, "end": v(-14.32, 7.7) * mm});
            skLineSegment(sketch, "E328", {"start": v(-9.17, -2.06) * mm, "end": v(-8.37, -2.06) * mm});
            skLineSegment(sketch, "E329", {"start": v(-8.37, -2.06) * mm, "end": v(-8.37, -2.96) * mm});
            skLineSegment(sketch, "E330", {"start": v(-8.37, -2.96) * mm, "end": v(-9.17, -2.96) * mm});
            skLineSegment(sketch, "E331", {"start": v(-9.17, -2.96) * mm, "end": v(-9.17, -2.06) * mm});
            skLineSegment(sketch, "E332", {"start": v(-8.22, -4.16) * mm, "end": v(-7.42, -4.16) * mm});
            skLineSegment(sketch, "E333", {"start": v(-7.42, -4.16) * mm, "end": v(-7.42, -5.06) * mm});
            skLineSegment(sketch, "E334", {"start": v(-7.42, -5.06) * mm, "end": v(-8.22, -5.06) * mm});
            skLineSegment(sketch, "E335", {"start": v(-8.22, -5.06) * mm, "end": v(-8.22, -4.16) * mm});
            skLineSegment(sketch, "E336", {"start": v(-7.27, -2.06) * mm, "end": v(-6.47, -2.06) * mm});
            skLineSegment(sketch, "E337", {"start": v(-6.47, -2.06) * mm, "end": v(-6.47, -2.96) * mm});
            skLineSegment(sketch, "E338", {"start": v(-6.47, -2.96) * mm, "end": v(-7.27, -2.96) * mm});
            skLineSegment(sketch, "E339", {"start": v(-7.27, -2.96) * mm, "end": v(-7.27, -2.06) * mm});
            skLineSegment(sketch, "E340", {"start": v(4.17, -10.7) * mm, "end": v(4.97, -10.7) * mm});
            skLineSegment(sketch, "E341", {"start": v(4.97, -10.7) * mm, "end": v(4.97, -11.6) * mm});
            skLineSegment(sketch, "E342", {"start": v(4.97, -11.6) * mm, "end": v(4.17, -11.6) * mm});
            skLineSegment(sketch, "E343", {"start": v(4.17, -11.6) * mm, "end": v(4.17, -10.7) * mm});
            skLineSegment(sketch, "E344", {"start": v(6.07, -10.7) * mm, "end": v(6.87, -10.7) * mm});
            skLineSegment(sketch, "E345", {"start": v(6.87, -10.7) * mm, "end": v(6.87, -11.6) * mm});
            skLineSegment(sketch, "E346", {"start": v(6.87, -11.6) * mm, "end": v(6.07, -11.6) * mm});
            skLineSegment(sketch, "E347", {"start": v(6.07, -11.6) * mm, "end": v(6.07, -10.7) * mm});
            skLineSegment(sketch, "E348", {"start": v(5.12, -12.8) * mm, "end": v(5.92, -12.8) * mm});
            skLineSegment(sketch, "E349", {"start": v(5.92, -12.8) * mm, "end": v(5.92, -13.7) * mm});
            skLineSegment(sketch, "E350", {"start": v(5.92, -13.7) * mm, "end": v(5.12, -13.7) * mm});
            skLineSegment(sketch, "E351", {"start": v(5.12, -13.7) * mm, "end": v(5.12, -12.8) * mm});
            skLineSegment(sketch, "E352", {"start": v(12.08, 0.44) * mm, "end": v(13.98, 0.44) * mm});
            skLineSegment(sketch, "E353", {"start": v(13.98, 0.44) * mm, "end": v(13.98, 0.1) * mm});
            skLineSegment(sketch, "E354", {"start": v(13.98, 0.1) * mm, "end": v(12.08, 0.1) * mm});
            skLineSegment(sketch, "E355", {"start": v(12.08, 0.1) * mm, "end": v(12.08, 0.44) * mm});
            skLineSegment(sketch, "E356", {"start": v(12.08, 1.1) * mm, "end": v(13.98, 1.1) * mm});
            skLineSegment(sketch, "E357", {"start": v(13.98, 1.1) * mm, "end": v(13.98, 0.76) * mm});
            skLineSegment(sketch, "E358", {"start": v(13.98, 0.76) * mm, "end": v(12.08, 0.76) * mm});
            skLineSegment(sketch, "E359", {"start": v(12.08, 0.76) * mm, "end": v(12.08, 1.1) * mm});
            skLineSegment(sketch, "E360", {"start": v(12.08, 1.74) * mm, "end": v(13.98, 1.74) * mm});
            skLineSegment(sketch, "E361", {"start": v(13.98, 1.74) * mm, "end": v(13.98, 1.41) * mm});
            skLineSegment(sketch, "E362", {"start": v(13.98, 1.41) * mm, "end": v(12.08, 1.41) * mm});
            skLineSegment(sketch, "E363", {"start": v(12.08, 1.41) * mm, "end": v(12.08, 1.74) * mm});
            skLineSegment(sketch, "E364", {"start": v(12.08, 2.4) * mm, "end": v(13.98, 2.4) * mm});
            skLineSegment(sketch, "E365", {"start": v(13.98, 2.4) * mm, "end": v(13.98, 2.06) * mm});
            skLineSegment(sketch, "E366", {"start": v(13.98, 2.06) * mm, "end": v(12.08, 2.06) * mm});
            skLineSegment(sketch, "E367", {"start": v(12.08, 2.06) * mm, "end": v(12.08, 2.4) * mm});
            skLineSegment(sketch, "E368", {"start": v(12.08, 3.04) * mm, "end": v(13.98, 3.04) * mm});
            skLineSegment(sketch, "E369", {"start": v(13.98, 3.04) * mm, "end": v(13.98, 2.71) * mm});
            skLineSegment(sketch, "E370", {"start": v(13.98, 2.71) * mm, "end": v(12.08, 2.71) * mm});
            skLineSegment(sketch, "E371", {"start": v(12.08, 2.71) * mm, "end": v(12.08, 3.04) * mm});
            skLineSegment(sketch, "E372", {"start": v(14.73, 6.48) * mm, "end": v(16.63, 6.48) * mm});
            skLineSegment(sketch, "E373", {"start": v(16.63, 6.48) * mm, "end": v(16.63, 4.68) * mm});
            skLineSegment(sketch, "E374", {"start": v(16.63, 4.68) * mm, "end": v(14.73, 4.68) * mm});
            skLineSegment(sketch, "E375", {"start": v(14.73, 4.68) * mm, "end": v(14.73, 6.48) * mm});
            skLineSegment(sketch, "E376", {"start": v(14.73, -1.53) * mm, "end": v(16.63, -1.53) * mm});
            skLineSegment(sketch, "E377", {"start": v(16.63, -1.53) * mm, "end": v(16.63, -3.33) * mm});
            skLineSegment(sketch, "E378", {"start": v(16.63, -3.33) * mm, "end": v(14.73, -3.33) * mm});
            skLineSegment(sketch, "E379", {"start": v(14.73, -3.33) * mm, "end": v(14.73, -1.53) * mm});
            skLineSegment(sketch, "E380", {"start": v(14.73, 1.26) * mm, "end": v(16.63, 1.26) * mm});
            skLineSegment(sketch, "E381", {"start": v(16.63, 1.26) * mm, "end": v(16.63, -0.65) * mm});
            skLineSegment(sketch, "E382", {"start": v(16.63, -0.65) * mm, "end": v(14.73, -0.65) * mm});
            skLineSegment(sketch, "E383", {"start": v(14.73, -0.65) * mm, "end": v(14.73, 1.26) * mm});
            skLineSegment(sketch, "E384", {"start": v(14.73, 3.8) * mm, "end": v(16.63, 3.8) * mm});
            skLineSegment(sketch, "E385", {"start": v(16.63, 3.8) * mm, "end": v(16.63, 1.9) * mm});
            skLineSegment(sketch, "E386", {"start": v(16.63, 1.9) * mm, "end": v(14.73, 1.9) * mm});
            skLineSegment(sketch, "E387", {"start": v(14.73, 1.9) * mm, "end": v(14.73, 3.8) * mm});
            skLineSegment(sketch, "E388", {"start": v(12.33, 5.73) * mm, "end": v(13.93, 5.73) * mm});
            skLineSegment(sketch, "E389", {"start": v(13.93, 5.73) * mm, "end": v(13.93, 3.63) * mm});
            skLineSegment(sketch, "E390", {"start": v(13.93, 3.63) * mm, "end": v(12.33, 3.63) * mm});
            skLineSegment(sketch, "E391", {"start": v(12.33, 3.63) * mm, "end": v(12.33, 5.73) * mm});
            skLineSegment(sketch, "E392", {"start": v(12.33, -0.48) * mm, "end": v(13.93, -0.48) * mm});
            skLineSegment(sketch, "E393", {"start": v(13.93, -0.48) * mm, "end": v(13.93, -2.58) * mm});
            skLineSegment(sketch, "E394", {"start": v(13.93, -2.58) * mm, "end": v(12.33, -2.58) * mm});
            skLineSegment(sketch, "E395", {"start": v(12.33, -2.58) * mm, "end": v(12.33, -0.48) * mm});
            skLineSegment(sketch, "E396", {"start": v(2.02, 14.6) * mm, "end": v(9.02, 14.6) * mm});
            skLineSegment(sketch, "E397", {"start": v(9.02, 14.6) * mm, "end": v(9.02, 7.6) * mm});
            skLineSegment(sketch, "E398", {"start": v(9.02, 7.6) * mm, "end": v(2.02, 7.6) * mm});
            skLineSegment(sketch, "E399", {"start": v(2.02, 7.6) * mm, "end": v(2.02, 14.6) * mm});
            skLineSegment(sketch, "E400", {"start": v(-9.42, 14.6) * mm, "end": v(-2.41, 14.6) * mm});
            skLineSegment(sketch, "E401", {"start": v(-2.41, 14.6) * mm, "end": v(-2.41, 7.6) * mm});
            skLineSegment(sketch, "E402", {"start": v(-2.41, 7.6) * mm, "end": v(-9.42, 7.6) * mm});
            skLineSegment(sketch, "E403", {"start": v(-9.42, 7.6) * mm, "end": v(-9.42, 14.6) * mm});
            skLineSegment(sketch, "E404", {"start": v(-12.45, 9.43) * mm, "end": v(-11.45, 9.43) * mm});
            skLineSegment(sketch, "E405", {"start": v(-11.45, 9.43) * mm, "end": v(-11.45, 8.03) * mm});
            skLineSegment(sketch, "E406", {"start": v(-11.45, 8.03) * mm, "end": v(-12.45, 8.03) * mm});
            skLineSegment(sketch, "E407", {"start": v(-12.45, 8.03) * mm, "end": v(-12.45, 9.43) * mm});
            skLineSegment(sketch, "E408", {"start": v(-14.36, 9.43) * mm, "end": v(-13.35, 9.43) * mm});
            skLineSegment(sketch, "E409", {"start": v(-13.35, 9.43) * mm, "end": v(-13.35, 8.03) * mm});
            skLineSegment(sketch, "E410", {"start": v(-13.35, 8.03) * mm, "end": v(-14.36, 8.03) * mm});
            skLineSegment(sketch, "E411", {"start": v(-14.36, 8.03) * mm, "end": v(-14.36, 9.43) * mm});
            skLineSegment(sketch, "E412", {"start": v(-13.4, 11.63) * mm, "end": v(-12.4, 11.63) * mm});
            skLineSegment(sketch, "E413", {"start": v(-12.4, 11.63) * mm, "end": v(-12.4, 10.23) * mm});
            skLineSegment(sketch, "E414", {"start": v(-12.4, 10.23) * mm, "end": v(-13.4, 10.23) * mm});
            skLineSegment(sketch, "E415", {"start": v(-13.4, 10.23) * mm, "end": v(-13.4, 11.63) * mm});
            skLineSegment(sketch, "E416", {"start": v(-3.64, -6.38) * mm, "end": v(-2.14, -6.38) * mm});
            skLineSegment(sketch, "E417", {"start": v(-2.14, -6.38) * mm, "end": v(-2.14, -6.98) * mm});
            skLineSegment(sketch, "E418", {"start": v(-2.14, -6.98) * mm, "end": v(-3.64, -6.98) * mm});
            skLineSegment(sketch, "E419", {"start": v(-3.64, -6.98) * mm, "end": v(-3.64, -6.38) * mm});
            skLineSegment(sketch, "E420", {"start": v(-3.64, -7.65) * mm, "end": v(-2.14, -7.65) * mm});
            skLineSegment(sketch, "E421", {"start": v(-2.14, -7.65) * mm, "end": v(-2.14, -8.25) * mm});
            skLineSegment(sketch, "E422", {"start": v(-2.14, -8.25) * mm, "end": v(-3.64, -8.25) * mm});
            skLineSegment(sketch, "E423", {"start": v(-3.64, -8.25) * mm, "end": v(-3.64, -7.65) * mm});
            skLineSegment(sketch, "E424", {"start": v(-3.64, -8.92) * mm, "end": v(-2.14, -8.92) * mm});
            skLineSegment(sketch, "E425", {"start": v(-2.14, -8.92) * mm, "end": v(-2.14, -9.52) * mm});
            skLineSegment(sketch, "E426", {"start": v(-2.14, -9.52) * mm, "end": v(-3.64, -9.52) * mm});
            skLineSegment(sketch, "E427", {"start": v(-3.64, -9.52) * mm, "end": v(-3.64, -8.92) * mm});
            skLineSegment(sketch, "E428", {"start": v(-3.64, -10.2) * mm, "end": v(-2.14, -10.2) * mm});
            skLineSegment(sketch, "E429", {"start": v(-2.14, -10.2) * mm, "end": v(-2.14, -10.8) * mm});
            skLineSegment(sketch, "E430", {"start": v(-2.14, -10.8) * mm, "end": v(-3.64, -10.8) * mm});
            skLineSegment(sketch, "E431", {"start": v(-3.64, -10.8) * mm, "end": v(-3.64, -10.2) * mm});
            skLineSegment(sketch, "E432", {"start": v(-3.64, -11.46) * mm, "end": v(-2.14, -11.46) * mm});
            skLineSegment(sketch, "E433", {"start": v(-2.14, -11.46) * mm, "end": v(-2.14, -12.06) * mm});
            skLineSegment(sketch, "E434", {"start": v(-2.14, -12.06) * mm, "end": v(-3.64, -12.06) * mm});
            skLineSegment(sketch, "E435", {"start": v(-3.64, -12.06) * mm, "end": v(-3.64, -11.46) * mm});
            skLineSegment(sketch, "E436", {"start": v(-3.64, -12.73) * mm, "end": v(-2.14, -12.73) * mm});
            skLineSegment(sketch, "E437", {"start": v(-2.14, -12.73) * mm, "end": v(-2.14, -13.33) * mm});
            skLineSegment(sketch, "E438", {"start": v(-2.14, -13.33) * mm, "end": v(-3.64, -13.33) * mm});
            skLineSegment(sketch, "E439", {"start": v(-3.64, -13.33) * mm, "end": v(-3.64, -12.73) * mm});
            skLineSegment(sketch, "E440", {"start": v(-3.64, -14) * mm, "end": v(-2.14, -14) * mm});
            skLineSegment(sketch, "E441", {"start": v(-2.14, -14) * mm, "end": v(-2.14, -14.6) * mm});
            skLineSegment(sketch, "E442", {"start": v(-2.14, -14.6) * mm, "end": v(-3.64, -14.6) * mm});
            skLineSegment(sketch, "E443", {"start": v(-3.64, -14.6) * mm, "end": v(-3.64, -14) * mm});
            skLineSegment(sketch, "E444", {"start": v(1.74, -14) * mm, "end": v(3.24, -14) * mm});
            skLineSegment(sketch, "E445", {"start": v(3.24, -14) * mm, "end": v(3.24, -14.6) * mm});
            skLineSegment(sketch, "E446", {"start": v(3.24, -14.6) * mm, "end": v(1.74, -14.6) * mm});
            skLineSegment(sketch, "E447", {"start": v(1.74, -14.6) * mm, "end": v(1.74, -14) * mm});
            skLineSegment(sketch, "E448", {"start": v(1.74, -12.73) * mm, "end": v(3.24, -12.73) * mm});
            skLineSegment(sketch, "E449", {"start": v(3.24, -12.73) * mm, "end": v(3.24, -13.33) * mm});
            skLineSegment(sketch, "E450", {"start": v(3.24, -13.33) * mm, "end": v(1.74, -13.33) * mm});
            skLineSegment(sketch, "E451", {"start": v(1.74, -13.33) * mm, "end": v(1.74, -12.73) * mm});
            skLineSegment(sketch, "E452", {"start": v(1.74, -11.46) * mm, "end": v(3.24, -11.46) * mm});
            skLineSegment(sketch, "E453", {"start": v(3.24, -11.46) * mm, "end": v(3.24, -12.06) * mm});
            skLineSegment(sketch, "E454", {"start": v(3.24, -12.06) * mm, "end": v(1.74, -12.06) * mm});
            skLineSegment(sketch, "E455", {"start": v(1.74, -12.06) * mm, "end": v(1.74, -11.46) * mm});
            skLineSegment(sketch, "E456", {"start": v(1.74, -10.2) * mm, "end": v(3.24, -10.2) * mm});
            skLineSegment(sketch, "E457", {"start": v(3.24, -10.2) * mm, "end": v(3.24, -10.8) * mm});
            skLineSegment(sketch, "E458", {"start": v(3.24, -10.8) * mm, "end": v(1.74, -10.8) * mm});
            skLineSegment(sketch, "E459", {"start": v(1.74, -10.8) * mm, "end": v(1.74, -10.2) * mm});
            skLineSegment(sketch, "E460", {"start": v(1.74, -8.92) * mm, "end": v(3.24, -8.92) * mm});
            skLineSegment(sketch, "E461", {"start": v(3.24, -8.92) * mm, "end": v(3.24, -9.52) * mm});
            skLineSegment(sketch, "E462", {"start": v(3.24, -9.52) * mm, "end": v(1.74, -9.52) * mm});
            skLineSegment(sketch, "E463", {"start": v(1.74, -9.52) * mm, "end": v(1.74, -8.92) * mm});
            skLineSegment(sketch, "E464", {"start": v(1.74, -7.65) * mm, "end": v(3.24, -7.65) * mm});
            skLineSegment(sketch, "E465", {"start": v(3.24, -7.65) * mm, "end": v(3.24, -8.25) * mm});
            skLineSegment(sketch, "E466", {"start": v(3.24, -8.25) * mm, "end": v(1.74, -8.25) * mm});
            skLineSegment(sketch, "E467", {"start": v(1.74, -8.25) * mm, "end": v(1.74, -7.65) * mm});
            skLineSegment(sketch, "E468", {"start": v(1.74, -6.38) * mm, "end": v(3.24, -6.38) * mm});
            skLineSegment(sketch, "E469", {"start": v(3.24, -6.38) * mm, "end": v(3.24, -6.98) * mm});
            skLineSegment(sketch, "E470", {"start": v(3.24, -6.98) * mm, "end": v(1.74, -6.98) * mm});
            skLineSegment(sketch, "E471", {"start": v(1.74, -6.98) * mm, "end": v(1.74, -6.38) * mm});
            skLineSegment(sketch, "E472", {"start": v(3.63, 4.69) * mm, "end": v(4.23, 4.69) * mm});
            skLineSegment(sketch, "E473", {"start": v(4.23, 4.69) * mm, "end": v(4.23, 3.49) * mm});
            skLineSegment(sketch, "E474", {"start": v(4.23, 3.49) * mm, "end": v(3.63, 3.49) * mm});
            skLineSegment(sketch, "E475", {"start": v(3.63, 3.49) * mm, "end": v(3.63, 4.69) * mm});
            skLineSegment(sketch, "E476", {"start": v(4.58, 4.69) * mm, "end": v(5.18, 4.69) * mm});
            skLineSegment(sketch, "E477", {"start": v(5.18, 4.69) * mm, "end": v(5.18, 3.49) * mm});
            skLineSegment(sketch, "E478", {"start": v(5.18, 3.49) * mm, "end": v(4.58, 3.49) * mm});
            skLineSegment(sketch, "E479", {"start": v(4.58, 3.49) * mm, "end": v(4.58, 4.69) * mm});
            skLineSegment(sketch, "E480", {"start": v(5.53, 4.69) * mm, "end": v(6.13, 4.69) * mm});
            skLineSegment(sketch, "E481", {"start": v(6.13, 4.69) * mm, "end": v(6.13, 3.49) * mm});
            skLineSegment(sketch, "E482", {"start": v(6.13, 3.49) * mm, "end": v(5.53, 3.49) * mm});
            skLineSegment(sketch, "E483", {"start": v(5.53, 3.49) * mm, "end": v(5.53, 4.69) * mm});
            skLineSegment(sketch, "E484", {"start": v(5.53, 7.29) * mm, "end": v(6.13, 7.29) * mm});
            skLineSegment(sketch, "E485", {"start": v(6.13, 7.29) * mm, "end": v(6.13, 6.09) * mm});
            skLineSegment(sketch, "E486", {"start": v(6.13, 6.09) * mm, "end": v(5.53, 6.09) * mm});
            skLineSegment(sketch, "E487", {"start": v(5.53, 6.09) * mm, "end": v(5.53, 7.29) * mm});
            skLineSegment(sketch, "E488", {"start": v(3.63, 7.29) * mm, "end": v(4.23, 7.29) * mm});
            skLineSegment(sketch, "E489", {"start": v(4.23, 7.29) * mm, "end": v(4.23, 6.09) * mm});
            skLineSegment(sketch, "E490", {"start": v(4.23, 6.09) * mm, "end": v(3.63, 6.09) * mm});
            skLineSegment(sketch, "E491", {"start": v(3.63, 6.09) * mm, "end": v(3.63, 7.29) * mm});
            skCircle(sketch, "E492", {"center": v(0, 0) * mm, "radius": 22.62 * mm});
            skSolve(sketch);
        }
        {
            var Q0;
            Q0 = qSketchRegion(id + "F0", true);
            extrude(context, id + "F1", {"entities" : qUnion([Q0]), "depth" : 1 * mm});
        }
    });
